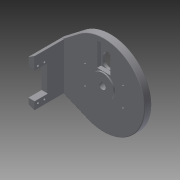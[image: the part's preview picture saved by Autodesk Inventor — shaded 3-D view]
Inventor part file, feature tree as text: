
AUTODESK INVENTOR PART (.ipt)
format: ipt  version: 2015 (Build 190159000, 159)  size: 440,320 bytes
history: native  units: mm
features: sketch x24, extrude x22, fillet x4
ambient origin geometry x8: Origin, YZ Plane, XZ Plane, XY Plane, X Axis, Y Axis, Z Axis, Center Point
bodies: Solid1 (feature_tree)
feature tree (50):
  extrude  "Extrusion1"  Depth=6.0mm
  extrude  "Extrusion2"  Depth=10.0mm
  extrude  "Extrusion3"  Depth=24.3mm
  extrude  "Extrusion4"  Depth=10.0mm
  sketch  "Sketch5"  dims[d9=60.0mm d10=60.0mm]
  extrude  "Extrusion5"  Depth=60.0mm
  extrude  "Extrusion6"  Depth=15.0mm
  extrude  "Extrusion7"  Depth=15.0mm
  extrude  "Extrusion8"  Depth=3.0mm
  extrude  "Extrusion9"  Depth=3.0mm
  extrude  "Extrusion10"  Depth=10.0mm
  extrude  "Extrusion11"  Depth=55.0mm
  extrude  "Extrusion12"  Depth=10.0mm
  extrude  "Extrusion13"  Depth=5.0mm TaperAngle=0.0deg
  extrude  "Extrusion22"  Depth=4.0mm
  sketch  "Sketch24"  dims[d47=10.0mm d48=0.0mm d49=48.0mm d50=0.0mm]
  sketch  "Sketch25"  dims[d51=35.0mm d54=34.25mm]
  extrude  "Extrusion23"  Depth=10.0mm TaperAngle=0.0deg
  extrude  "Extrusion24"  Depth=34.25mm
  sketch  "Sketch29"  dims[d60=3.0mm d61=3.0mm]
  extrude  "Extrusion27"  Depth=40.2mm
  extrude  "Extrusion28"  Depth=3.0mm
  extrude  "Extrusion29"  Depth=3.0mm
  extrude  "Extrusion32"  Depth=10.0mm TaperAngle=0.0deg
  extrude  "Extrusion37"  Depth=4.0mm
  extrude  "Extrusion38"  Depth=10.0mm
  fillet  "Fillet10"  Radius=10.0mm
  fillet  "Fillet11"  Radius=15.0mm
  fillet  "Fillet12"  Radius=10.0mm
  fillet  "Fillet13"  Radius=6.0mm
  sketch  "Sketch1"  dims[d0=120.0mm d1=6.0mm]
  sketch  "Sketch2"  dims[d2=10.0mm d3=0.0mm d4=24.3mm]
  sketch  "Sketch3"  dims[d5=5.0mm d6=24.3mm]
  sketch  "Sketch4"  dims[d7=5.0mm d8=10.0mm]
  sketch  "Sketch6"  dims[d11=15.0mm d12=15.0mm]
  sketch  "Sketch7"  dims[d13=15.0mm d14=15.0mm]
  sketch  "Sketch8"  dims[d15=3.0mm d16=3.0mm]
  sketch  "Sketch9"  dims[d17=3.0mm d18=3.0mm]
  sketch  "Sketch10"  dims[d19=10.0mm d20=0.0mm d31=71.2mm]
  sketch  "Sketch11"  dims[d32=34.25mm d33=55.0mm]
  sketch  "Sketch12"  dims[d34=10.0mm d35=0.0mm d36=10.0mm]
  sketch  "Sketch14"  dims[d37=43.0mm d38=0.0mm d41=5.0mm d42=0.0mm]
  sketch  "Sketch23"  dims[d45=4.0mm d46=4.0mm]
  sketch  "Sketch26"  dims[d55=49.7mm d56=40.2mm]
  sketch  "Sketch30"  dims[d62=3.0mm d63=3.0mm]
  sketch  "Sketch31"  dims[d64=10.0mm d65=0.0mm d66=3.0mm d67=0.0mm]
  sketch  "Sketch32"  dims[d70=14.209mm d71=4.0mm]
  sketch  "Sketch35"  dims[d72=10.0mm d73=0.0mm d74=8.0mm d75=10.0mm d76=0.0mm d78=15.0mm d79=10.0mm d80=6.0mm d81=0.0mm]
  sketch  "Sketch40"  dims[d82=14.3mm]
  sketch  "Sketch41"  dims[d83=14.3mm d84=6.0mm d85=0.0mm d123=15.0mm d124=10.0mm d125=0.0mm d126=35.0mm d129=2.0mm d130=0.0mm d131=10.0mm d132=2.0mm d133=0.0mm d141=63.0mm d142=10.0mm d143=0.0mm d144=7.5mm d145=10.0mm d146=0.0mm d147=3.0mm d148=6.0mm d149=2.0mm d150=10.0mm d151=0.0mm d156=6.0mm d157=0.0mm d172=5.0mm d173=0.0mm d174=100.0mm d175=1.0mm d176=0.0mm d177=1.0mm d178=1.0mm d179=0.5mm d180=0.5mm]
